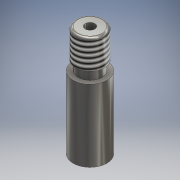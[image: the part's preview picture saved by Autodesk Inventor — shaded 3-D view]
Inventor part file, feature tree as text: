
AUTODESK INVENTOR PART (.ipt)
format: ipt  version: 2016 (Build 200138000, 138)  size: 135,680 bytes
history: native  units: mm
features: extrude x5, sketch x5, thread x1, fillet x1
ambient origin geometry x8: Origin, YZ Plane, XZ Plane, XY Plane, X Axis, Y Axis, Z Axis, Center Point
bodies: Solid1 (feature_tree)
feature tree (12):
  extrude  "Extrusion1"  Depth=15.0mm TaperAngle=0.0deg
  extrude  "Extrusion2"  Depth=2.0mm TaperAngle=0.0deg
  extrude  "Extrusion3"  Depth=6.0mm TaperAngle=0.0deg
  extrude  "Extrusion4"  Depth=6.0mm TaperAngle=0.0deg
  thread  "Thread1"  [1 undecoded]
  fillet  "Fillet1"  Radius=0.5mm
  extrude  "Extrusion5"  Depth=4.5mm TaperAngle=0.0deg
  sketch  "Sketch1"  dims[d0=7.0mm d1=15.0mm d2=0.0mm]
  sketch  "Sketch2"  dims[d3=5.0mm d4=2.0mm d5=0.0mm]
  sketch  "Sketch3"  dims[d6=6.0mm d7=6.0mm d8=0.0mm]
  sketch  "Sketch4"  dims[d9=2.0mm d10=6.0mm d11=0.0mm d12=10.0mm d13=0.0mm d14=0.5mm]
  sketch  "Sketch5"  dims[d15=4.2mm d16=4.5mm d17=0.0mm]
note: 1 required parameter value undecoded (feature->parameter linkage not recoverable at this tier; creation-order binding heuristic only, values carry confidence <= 0.55)
